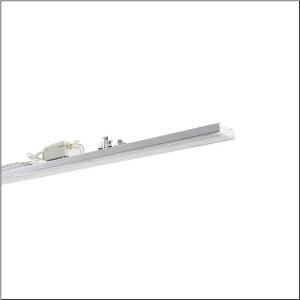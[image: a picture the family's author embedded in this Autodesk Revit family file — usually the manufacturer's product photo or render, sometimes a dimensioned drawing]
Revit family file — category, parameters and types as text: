
# Revit family: licross_r__11_recessed_mo_51tl147n48xg_3190
name_source: partatom
category: Lighting Fixtures
units: mm (PartAtom-declared; Revit-internal decimal feet)

## family parameters
Cut with Voids When Loaded = No
Host = Face
Light Source = No
Part Type = Normal
Room Calculation Point = No
Round Connector Dimension = Use Diameter
Shared = No

## types (1)
- Licross® 11 Recessed MO (1 x LED, 8240 lm, 48.5 W, 4000K)
    Apparent Load = 49 VA
    CIE Flux Codes = 56 84 97 100 100
    Color Rendering = 80
    Color Temperature = 4000K
    Default Elevation = 1800 mm
    Description = Licross® 11 Recessed MO, luminaire insert, of sheet steel, coil coated, white, length: 1.500mm, width: 66mm, height: 67mm, LED rated luminous flux: 8.240lm, light colour: 840, SDCM (Standard Deviation of Colour Matching)MacAdam ≤ 2 SDCM (initial), control gear: ON/OFF, with plug, 3-pole, with phase selection, mains connection: 220..240V, AC, 50/60Hz, rated input power: 49W, internal wiring halogen-free, primary light control with lens, of plastic, primary optical cover: cover, of PMMA, light emission: direct distribution, primary light characteristic: asymmetric, protection rating (complete): IP40, insulation class (complete): insulation class I (protective earthing), certification: CE, ENEC, VDE, UKCA, protection symbol: D if used in an environment without relevant dust loads with corresponding accessories, impact resistance: IK06, permissible ambient temperature for indoor applications: -35..+35°C, corresponds to IFS (International Featured Standards) requirements for safety and quality in the food industry, reducing of maximum allowable ambient temperature of 5°C with ceiling mounting, packaging unit: 1 piece
    Height = 58 mm
    Lamp = 1 x LED
    Lamp Light Flux = 8240 lm
    Lamp Power = 48.5 W
    Lamp count = 1
    Length = 1500 mm
    Luminous efficacy = 170 lm/W
    Manufacturer = Siteco
    ModVariant = No
    Model = 51TL147N48XG
    Mounting Place = Ceiling
    Mounting Type = Pendant
    Number of Poles = 1
    OnlyDefault = Yes
    Power Factor = 1
    Product Name = Licross® 11 Recessed MO
    Product group = luminaire insert | ceiling pendant
    ProductGroupID = 901
    Protection Class = Protection class I
    Protection Degree = IP 40
    RLX_Detail_Level = 1
    RLX_Emergency_Light_Flux = 0 lm
    RLX_Emergency_Type = 0
    RLX_Emergency_Type_DB = No
    RlxData = <blob elided: 21393 chars, md5=ce37e3f3>
    Socket = socket
    Standby Power = 0 W
    System Light Flux = 8240 lm
    System Power = 49 W
    Type Comments = Product without accessories
    Type Image = l_1296930.jpg
    URL = http://relux.com
    VarID = ---
    Voltage = 0 V
    Weight = 0.00 kg
    Width = 66 mm

## geometry (parser evidence)
native form markers: Blend x4, Sweep x10
no freeform markers — native parametric forms only
